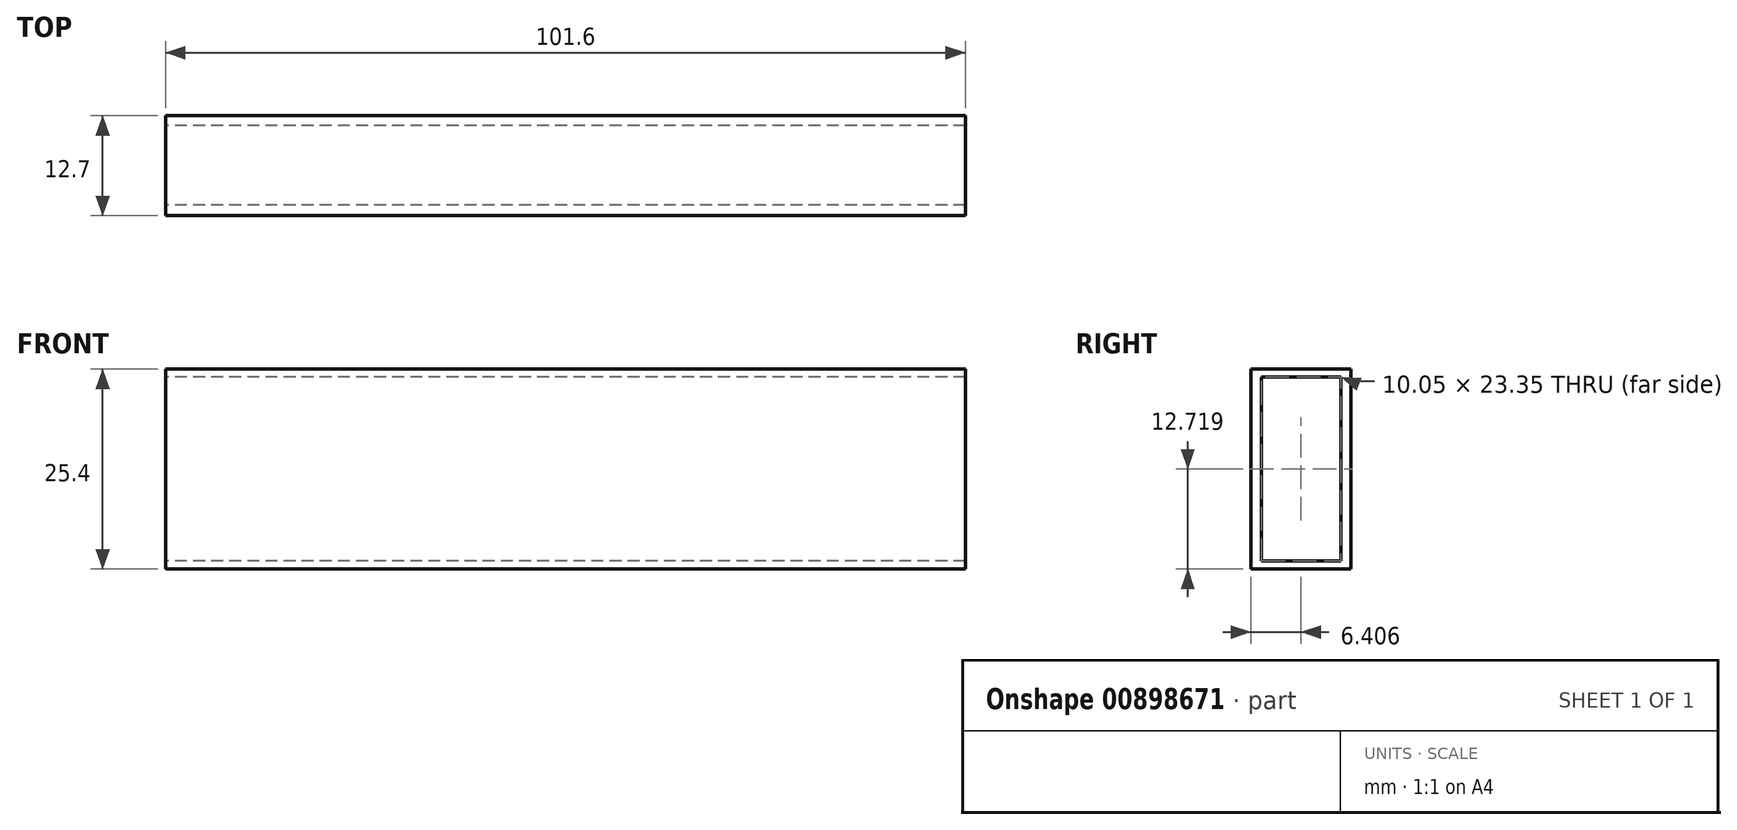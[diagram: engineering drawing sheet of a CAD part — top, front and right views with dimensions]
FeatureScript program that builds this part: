
annotation { "Feature Type Name" : "Feature", "Feature Type Description" : "" }
export const myFeature = defineFeature(function(context is Context, id is Id, definition is map)
    precondition{}
    {
        {
            var Q0;
            Q0=qCreatedBy(makeId("Top.planeOp"),FACE);
            var sketch = newSketch(context, id + "F0", { "sketchPlane" : qUnion([Q0])});
            skLineSegment(sketch, "E0.bottom", {"start": v(-60.72, 41.78) * mm, "end": v(40.88, 41.78) * mm});
            skLineSegment(sketch, "E0.top", {"start": v(-60.72, 29.08) * mm, "end": v(40.88, 29.08) * mm});
            skLineSegment(sketch, "E0.left", {"start": v(-60.72, 41.78) * mm, "end": v(-60.72, 29.08) * mm});
            skLineSegment(sketch, "E0.right", {"start": v(40.88, 41.78) * mm, "end": v(40.88, 29.08) * mm});
            skSolve(sketch);
        }
        {
            var Q0;
            Q0 = qSketchRegion(id + "F0", true);
            extrude(context, id + "F1", {"entities" : qUnion([Q0]), "depth" : 25.4 * mm, "offsetDistance" : 25.4 * mm});
        }
        {
            var Q0;
            Q0=makeQuery(id+"F1.opExtrude","SWEPT_FACE",FACE,{"disambiguationData":[OSD([sQuery(id+"F0.wireOp",EDGE,"E0.left")])]});
            var sketch = newSketch(context, id + "F2", { "sketchPlane" : qUnion([Q0])});
            skLineSegment(sketch, "E1.bottom", {"start": v(-30.46, 1.04) * mm, "end": v(-40.51, 1.04) * mm});
            skLineSegment(sketch, "E1.top", {"start": v(-30.46, 24.4) * mm, "end": v(-40.51, 24.4) * mm});
            skLineSegment(sketch, "E1.left", {"start": v(-30.46, 1.04) * mm, "end": v(-30.46, 24.4) * mm});
            skLineSegment(sketch, "E1.right", {"start": v(-40.51, 1.04) * mm, "end": v(-40.51, 24.4) * mm});
            skSolve(sketch);
        }
        {
            var Q0;
            Q0=makeQuery(id+"F2.imprint","IMPRINT",FACE,{"disambiguationData":[TD([[makeQuery(id+"F2.imprint","IMPRINT",EDGE,{"derivedFrom":sQuery(id+"F2.wireOp",EDGE,"E1.bottom")}),-1.0]])]});
            extrude(context, id + "F3", {"entities" : qUnion([Q0]), "operationType" : NewBodyOperationType.REMOVE, "oppositeDirection" : true, "depth" : 127 * mm, "offsetDistance" : 25.4 * mm, "hasSecondDirection" : true, "secondDirectionOppositeDirection" : false, "secondDirectionDepth" : 127 * mm});
        }
    });
